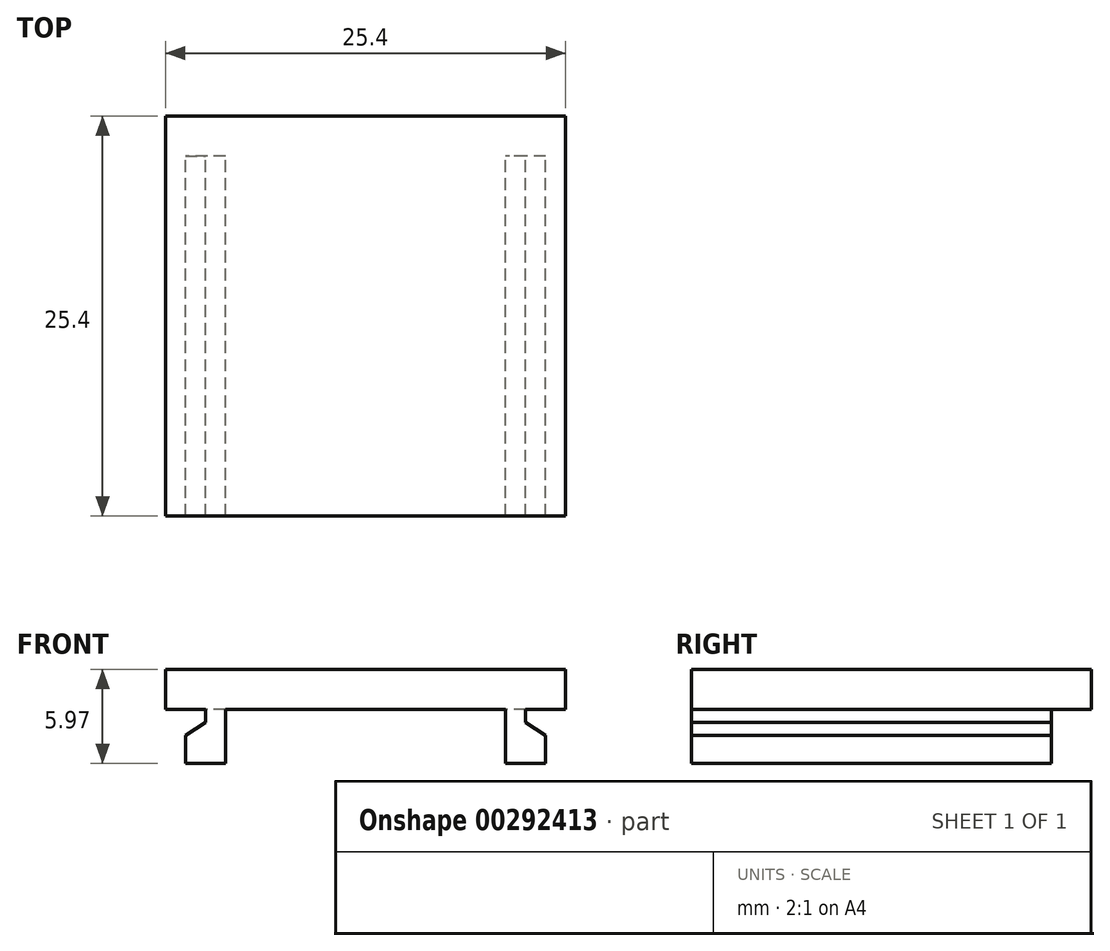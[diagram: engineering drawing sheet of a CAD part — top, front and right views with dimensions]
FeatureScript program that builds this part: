
annotation { "Feature Type Name" : "Feature", "Feature Type Description" : "" }
export const myFeature = defineFeature(function(context is Context, id is Id, definition is map)
    precondition{}
    {
        {
            var Q0;
            Q0=qCreatedBy(makeId("Top.planeOp"),FACE);
            var sketch = newSketch(context, id + "F0", { "sketchPlane" : qUnion([Q0])});
            skLineSegment(sketch, "E0.bottom", {"start": v(12.7, -12.7) * mm, "end": v(-12.7, -12.7) * mm});
            skLineSegment(sketch, "E0.top", {"start": v(12.7, 12.7) * mm, "end": v(-12.7, 12.7) * mm});
            skLineSegment(sketch, "E0.left", {"start": v(12.7, -12.7) * mm, "end": v(12.7, 12.7) * mm});
            skLineSegment(sketch, "E0.right", {"start": v(-12.7, -12.7) * mm, "end": v(-12.7, 12.7) * mm});
            skPoint(sketch, "E0.middle", {"position": v(0, 0) * mm});
            skSolve(sketch);
        }
        {
            var Q0;
            Q0 = qSketchRegion(id + "F0", true);
            extrude(context, id + "F1", {"entities" : qUnion([Q0]), "oppositeDirection" : true, "depth" : 2.54 * mm});
        }
        {
            var Q0;
            Q0=qCreatedBy(makeId("Front.planeOp"),FACE);
            var sketch = newSketch(context, id + "F2", { "sketchPlane" : qUnion([Q0])});
            skLineSegment(sketch, "E1", {"start": v(-10.17, -2.54) * mm, "end": v(-10.17, -3.35) * mm});
            skLineSegment(sketch, "E2", {"start": v(10.17, -3.35) * mm, "end": v(10.17, -2.54) * mm});
            skLineSegment(sketch, "E3.bottom", {"start": v(-8.9, -5.97) * mm, "end": v(-11.44, -5.97) * mm});
            skLineSegment(sketch, "E3.right", {"start": v(-11.44, -5.97) * mm, "end": v(-11.44, -4.2) * mm});
            skLineSegment(sketch, "E4.bottom", {"start": v(11.44, -5.97) * mm, "end": v(8.9, -5.97) * mm});
            skLineSegment(sketch, "E4.left", {"start": v(11.44, -5.97) * mm, "end": v(11.44, -4.2) * mm});
            skLineSegment(sketch, "E5", {"start": v(-11.44, -4.2) * mm, "end": v(-10.17, -3.35) * mm});
            skLineSegment(sketch, "E6", {"start": v(11.44, -4.2) * mm, "end": v(10.17, -3.35) * mm});
            skLineSegment(sketch, "E7", {"start": v(-8.9, -2.54) * mm, "end": v(-10.17, -2.54) * mm});
            skLineSegment(sketch, "E8", {"start": v(8.9, -2.54) * mm, "end": v(10.17, -2.54) * mm});
            skLineSegment(sketch, "E9", {"start": v(-8.9, -5.97) * mm, "end": v(-8.9, -2.54) * mm});
            skLineSegment(sketch, "E10", {"start": v(8.9, -5.97) * mm, "end": v(8.9, -2.54) * mm});
            skSolve(sketch);
        }
        {
            var Q0;
            Q0=makeQuery(id+"F2.imprint","IMPRINT",FACE,{"disambiguationData":[TD([[makeQuery(id+"F2.imprint","IMPRINT",EDGE,{"derivedFrom":sQuery(id+"F2.wireOp",EDGE,"E1")}),1.0]])]});
            var Q1;
            Q1=makeQuery(id+"F2.imprint","IMPRINT",FACE,{"disambiguationData":[TD([[makeQuery(id+"F2.imprint","IMPRINT",EDGE,{"derivedFrom":sQuery(id+"F2.wireOp",EDGE,"E2")}),1.0]])]});
            extrude(context, id + "F3", {"entities" : qUnion([Q0, Q1]), "operationType" : NewBodyOperationType.ADD, "endBound" : BoundingType.SYMMETRIC, "depth" : 25.4 * mm});
        }
        {
            var Q0;
            Q0=qCreatedBy(makeId("Right.planeOp"),FACE);
            var sketch = newSketch(context, id + "F4", { "sketchPlane" : qUnion([Q0])});
            skLineSegment(sketch, "E11", {"start": v(0, 0) * mm, "end": v(0, -2.54) * mm});
            skLineSegment(sketch, "E12", {"start": v(12.7, -2.54) * mm, "end": v(12.7, -6.1) * mm});
            skLineSegment(sketch, "E13", {"start": v(12.7, -6.1) * mm, "end": v(10.16, -6.1) * mm});
            skLineSegment(sketch, "E14", {"start": v(10.16, -6.1) * mm, "end": v(10.16, -2.54) * mm});
            skLineSegment(sketch, "E15", {"start": v(10.16, -2.54) * mm, "end": v(12.7, -2.54) * mm});
            skSolve(sketch);
        }
        {
            var Q0;
            Q0 = qSketchRegion(id + "F4", true);
            extrude(context, id + "F5", {"entities" : qUnion([Q0]), "operationType" : NewBodyOperationType.REMOVE, "endBound" : BoundingType.SYMMETRIC, "depth" : 25.4 * mm});
        }
    });
